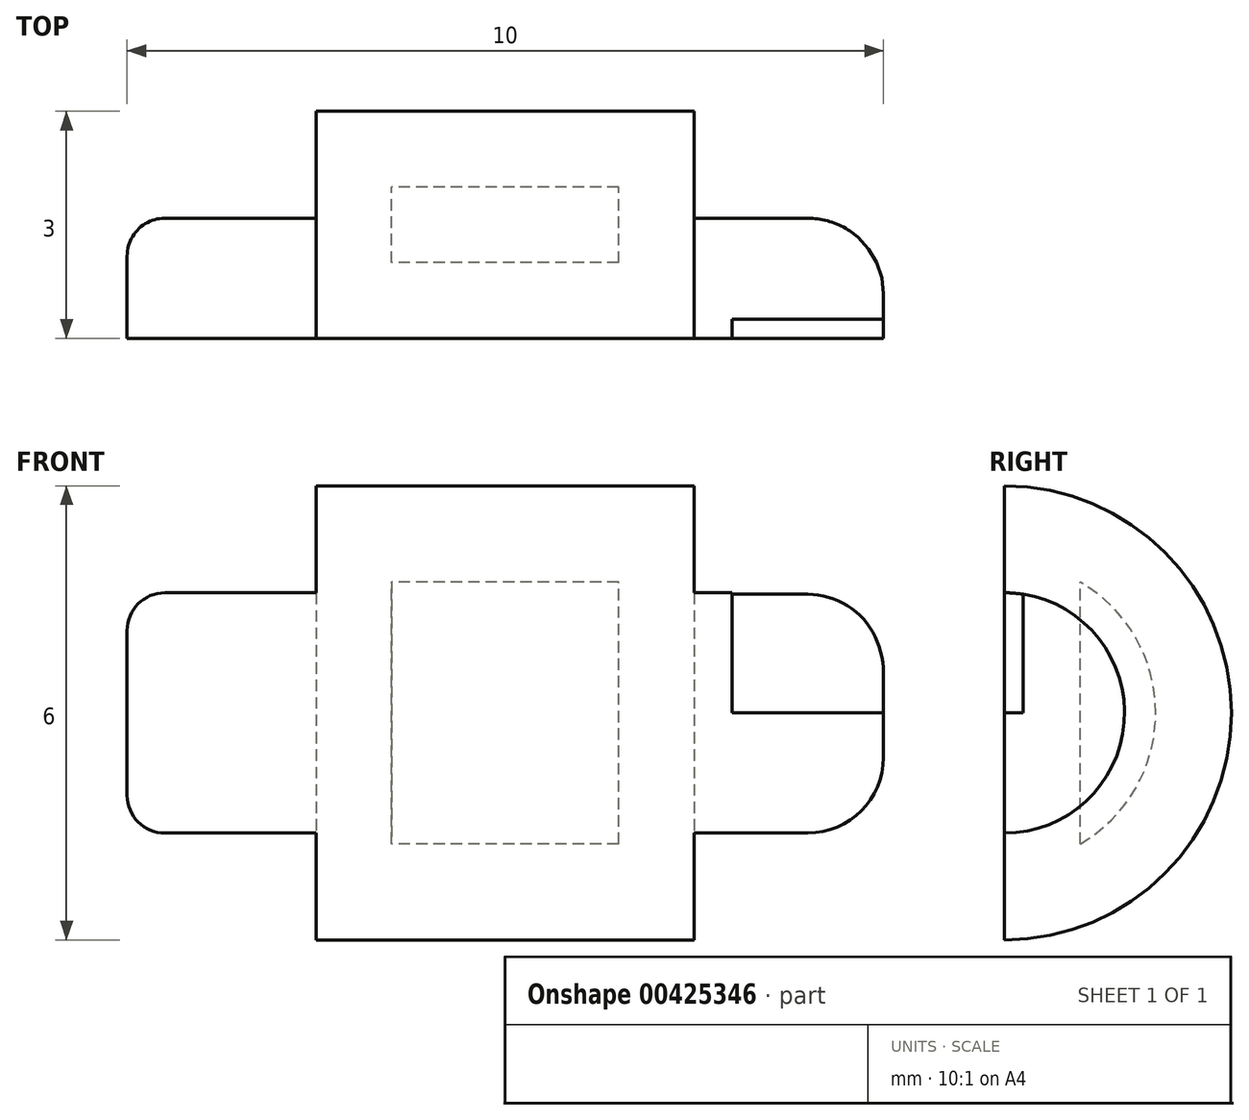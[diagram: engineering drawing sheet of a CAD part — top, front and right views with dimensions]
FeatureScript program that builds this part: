
annotation { "Feature Type Name" : "Feature", "Feature Type Description" : "" }
export const myFeature = defineFeature(function(context is Context, id is Id, definition is map)
    precondition{}
    {
        {
            var Q0;
            Q0=qCreatedBy(makeId("Top.planeOp"),FACE);
            var sketch = newSketch(context, id + "F0", { "sketchPlane" : qUnion([Q0])});
            skLineSegment(sketch, "E0", {"start": v(-3.83, 0) * mm, "end": v(4.32, 0) * mm, "construction": true});
            skLineSegment(sketch, "E1", {"start": v(-5, 1.59) * mm, "end": v(-2.5, 1.59) * mm});
            skLineSegment(sketch, "E2", {"start": v(-2.5, 1.59) * mm, "end": v(-2.5, 3) * mm});
            skLineSegment(sketch, "E3", {"start": v(-2.5, 3) * mm, "end": v(2.5, 3) * mm});
            skLineSegment(sketch, "E4", {"start": v(2.5, 3) * mm, "end": v(2.5, 1.59) * mm});
            skLineSegment(sketch, "E5", {"start": v(2.5, 1.59) * mm, "end": v(5, 1.59) * mm});
            skLineSegment(sketch, "E6", {"start": v(0, 0) * mm, "end": v(0, 5) * mm, "construction": true});
            skLineSegment(sketch, "E7", {"start": v(-5, 1.59) * mm, "end": v(-5, 0) * mm});
            skLineSegment(sketch, "E8", {"start": v(-5, 0) * mm, "end": v(5, 0) * mm});
            skLineSegment(sketch, "E9", {"start": v(5, 1.59) * mm, "end": v(5, 0) * mm});
            skSolve(sketch);
        }
        {
            var Q0;
            Q0=qSketchRegion(id+"F0",true);
            var Q1;
            Q1=sQuery(id+"F0.wireOp",EDGE,"E0");
            revolve(context, id + "F1", {"entities" : qUnion([Q0]), "axis" : qUnion([Q1]), "revolveType" : RevolveType.SYMMETRIC, "angle" : 180 * degree});
        }
        {
            var Q0;
            Q0=makeQuery(id+"F1.opRevolve","SWEPT_FACE",FACE,{"disambiguationData":[OSD([sQuery(id+"F0.wireOp",EDGE,"E9")])]});
            var Q1;
            Q1=makeQuery(id+"F1.opRevolve","SWEPT_FACE",FACE,{"disambiguationData":[OSD([sQuery(id+"F0.wireOp",EDGE,"E7")])]});
            shell(context, id + "F2", {"entities" : qUnion([Q0, Q1]), "thickness" : 1 * mm});
        }
        {
            var Q0;
            Q0=makeQuery(id+"F1.opRevolve","SWEPT_EDGE",EDGE,{"disambiguationData":[OSD([sQuery(id+"F0.wireOp",EDGE,"E5"),sQuery(id+"F0.wireOp",EDGE,"E9")])]});
            fillet(context, id + "F3", {"entities" : qUnion([Q0]), "radius" : 1 * mm, "tangentPropagation" : true, "allowEdgeOverflow" : false});
        }
        {
            var Q0;
            Q0=makeQuery(id+"F1.opRevolve","SWEPT_EDGE",EDGE,{"disambiguationData":[OSD([sQuery(id+"F0.wireOp",EDGE,"E1"),sQuery(id+"F0.wireOp",EDGE,"E7")])]});
            fillet(context, id + "F4", {"entities" : qUnion([Q0]), "radius" : 0.5 * mm, "tangentPropagation" : true, "allowEdgeOverflow" : false});
        }
        {
            var Q0;
            Q0=qCreatedBy(makeId("Top.planeOp"),FACE);
            var sketch = newSketch(context, id + "F5", { "sketchPlane" : qUnion([Q0])});
            skLineSegment(sketch, "E10", {"start": v(0, 0) * mm, "end": v(6.31, 0) * mm, "construction": true});
            skLineSegment(sketch, "E11.bottom", {"start": v(3, -0.25) * mm, "end": v(7, -0.25) * mm});
            skLineSegment(sketch, "E11.top", {"start": v(3, 0.25) * mm, "end": v(7, 0.25) * mm});
            skLineSegment(sketch, "E11.left", {"start": v(3, -0.25) * mm, "end": v(3, 0.25) * mm});
            skLineSegment(sketch, "E11.right", {"start": v(7, -0.25) * mm, "end": v(7, 0.25) * mm});
            skPoint(sketch, "E11.middle", {"position": v(5, 0) * mm});
            skSolve(sketch);
        }
        {
            var Q0;
            Q0=qSketchRegion(id+"F5",true);
            extrude(context, id + "F6", {"entities" : qUnion([Q0]), "operationType" : NewBodyOperationType.REMOVE, "depth" : 25 * mm, "offsetDistance" : 25 * mm});
        }
    });
